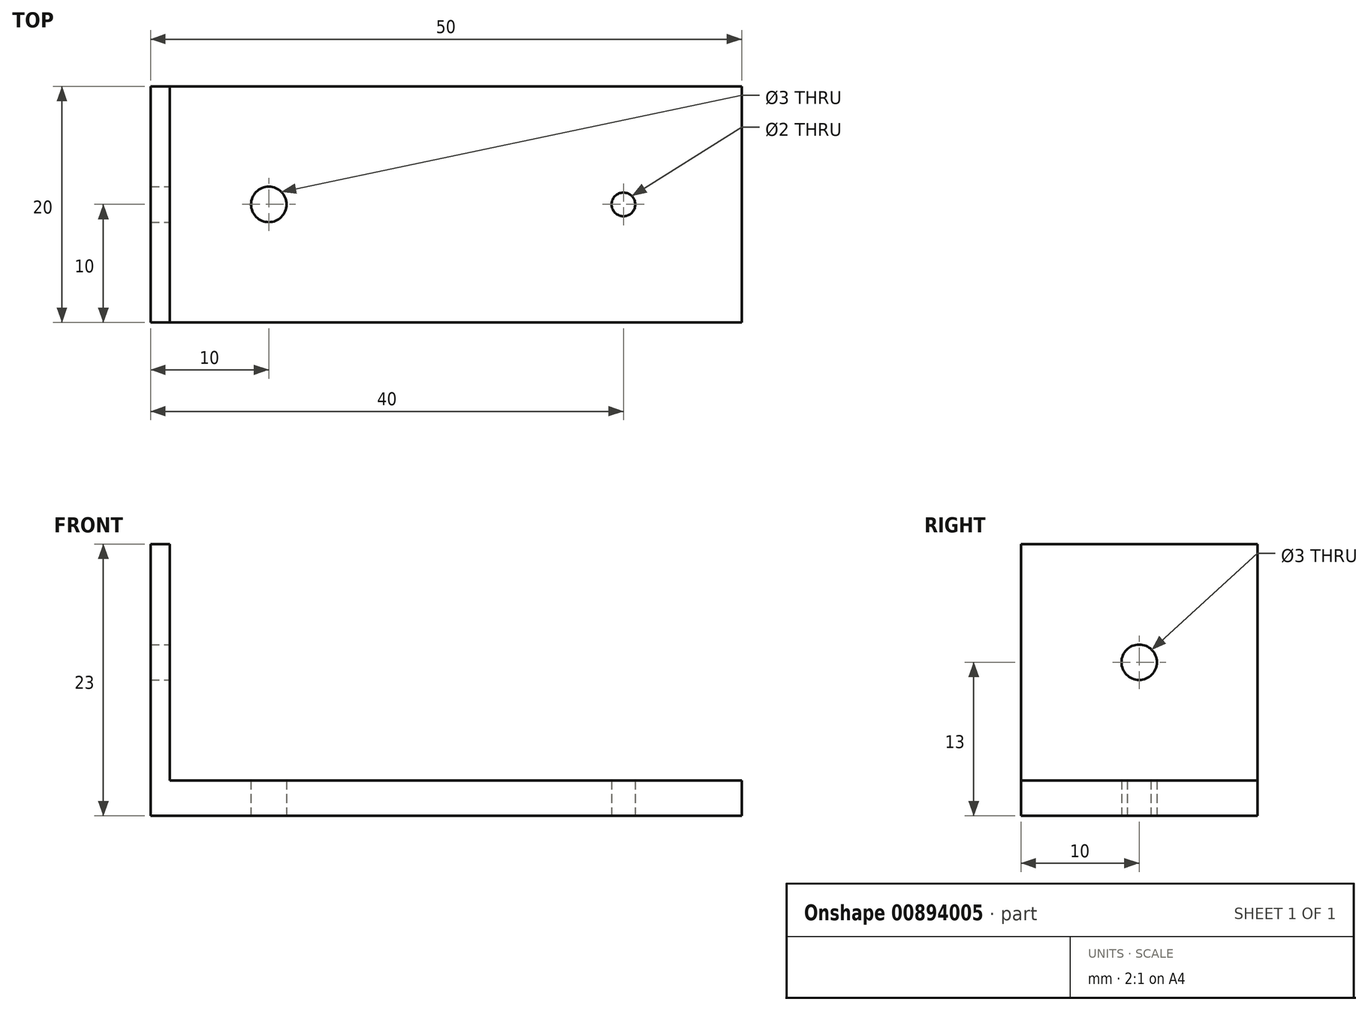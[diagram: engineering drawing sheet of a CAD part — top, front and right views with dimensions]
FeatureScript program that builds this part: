
annotation { "Feature Type Name" : "Feature", "Feature Type Description" : "" }
export const myFeature = defineFeature(function(context is Context, id is Id, definition is map)
    precondition{}
    {
        {
            var Q0;
            Q0=qCreatedBy(makeId("Top.planeOp"),FACE);
            var sketch = newSketch(context, id + "F0", { "sketchPlane" : qUnion([Q0])});
            skLineSegment(sketch, "E0.bottom", {"start": v(25, 10) * mm, "end": v(-25, 10) * mm});
            skLineSegment(sketch, "E0.top", {"start": v(25, -10) * mm, "end": v(-25, -10) * mm});
            skLineSegment(sketch, "E0.left", {"start": v(25, 10) * mm, "end": v(25, -10) * mm});
            skLineSegment(sketch, "E0.right", {"start": v(-25, 10) * mm, "end": v(-25, -10) * mm});
            skPoint(sketch, "E0.middle", {"position": v(0, 0) * mm});
            skCircle(sketch, "E1", {"center": v(-15, 0) * mm, "radius": 1.5 * mm});
            skCircle(sketch, "E2", {"center": v(15, 0) * mm, "radius": 1 * mm});
            skSolve(sketch);
        }
        {
            var Q0;
            {var subQ3=sQuery(id+"F0.wireOp",EDGE,"E0.bottom");Q0=makeQuery(id+"F0.imprint","IMPRINT",FACE,{"disambiguationData":[TD([[makeQuery(id+"F0.imprint","IMPRINT",EDGE,{"derivedFrom":subQ3}),1.0]])]});}
            extrude(context, id + "F1", {"entities" : qUnion([Q0]), "depth" : 3 * mm, "offsetDistance" : 25 * mm});
        }
        {
            var Q0;
            Q0=makeQuery(id+"F1.opExtrude","CAP_FACE",FACE,{"disambiguationData":[OSD([sQuery(id+"F0.wireOp",EDGE,"E0.bottom"),sQuery(id+"F0.wireOp",EDGE,"E0.top"),sQuery(id+"F0.wireOp",EDGE,"E0.left"),sQuery(id+"F0.wireOp",EDGE,"E0.right"),sQuery(id+"F0.wireOp",EDGE,"E1"),sQuery(id+"F0.wireOp",EDGE,"E2")])],"isStart":false});
            var sketch = newSketch(context, id + "F2", { "sketchPlane" : qUnion([Q0])});
            skLineSegment(sketch, "E3.bottom", {"start": v(-25, 10) * mm, "end": v(-23.36, 10) * mm});
            skLineSegment(sketch, "E3.top", {"start": v(-25, -10) * mm, "end": v(-23.36, -10) * mm});
            skLineSegment(sketch, "E3.left", {"start": v(-25, 10) * mm, "end": v(-25, -10) * mm});
            skLineSegment(sketch, "E3.right", {"start": v(-23.36, 10) * mm, "end": v(-23.36, -10) * mm});
            skPoint(sketch, "E3.middle", {"position": v(-24.18, 0) * mm});
            skPoint(sketch, "E3.middle.positionSnap0", {"position": v(-25, 0) * mm});
            skPoint(sketch, "E3.centerSnap0", {"position": v(-25, 0) * mm});
            skSolve(sketch);
        }
        {
            var Q0;
            Q0 = qSketchRegion(id + "F2", true);
            extrude(context, id + "F3", {"entities" : qUnion([Q0]), "operationType" : NewBodyOperationType.ADD, "depth" : 20 * mm, "offsetDistance" : 25 * mm});
        }
        {
            var Q0;
            Q0=makeQuery(id+"F3.opExtrude","SWEPT_FACE",FACE,{"disambiguationData":[OSD([sQuery(id+"F2.wireOp",EDGE,"E3.right")])]});
            var sketch = newSketch(context, id + "F4", { "sketchPlane" : qUnion([Q0])});
            skLineSegment(sketch, "E4", {"start": v(-10, 3) * mm, "end": v(-10, 23) * mm});
            skCircle(sketch, "E5", {"center": v(0, 13) * mm, "radius": 1.5 * mm});
            skSolve(sketch);
        }
        {
            var Q0;
            Q0=sQuery(id+"F4.wireOp",VERTEX,"E5.center");
            var Q1;
            Q1=makeQuery(id+"F1.opExtrude","SWEPT_BODY",BODY,{"disambiguationData":[OSD([sQuery(id+"F0.wireOp",EDGE,"E0.bottom"),sQuery(id+"F0.wireOp",EDGE,"E0.top"),sQuery(id+"F0.wireOp",EDGE,"E0.left"),sQuery(id+"F0.wireOp",EDGE,"E0.right"),sQuery(id+"F0.wireOp",EDGE,"E1"),sQuery(id+"F0.wireOp",EDGE,"E2")])]});
            hole(context, id + "F5", {"style" : HoleStyle.SIMPLE, "endStyle" : HoleEndStyle.THROUGH, "holeDiameter" : 3 * mm, "majorDiameter" : 5 * mm, "isTappedThrough" : true, "tappedDepth" : 12 * mm, "tapClearance" : 3, "locations" : qUnion([Q0]), "scope" : qUnion([Q1])});
        }
    });
